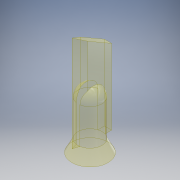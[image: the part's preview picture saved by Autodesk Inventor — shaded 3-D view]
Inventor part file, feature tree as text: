
AUTODESK INVENTOR PART (.ipt)
format: ipt  version: 2017 (Build 210142000, 142)  size: 141,824 bytes
history: native  units: mm
features: sketch x6, plane x3, extrude x3, loft x1, revolve x1
ambient origin geometry x8: Origin, YZ Plane, XZ Plane, XY Plane, X Axis, Y Axis, Z Axis, Center Point
bodies: Body1 (feature_tree)
feature tree (14):
  sketch  "Sketch1"  dims[d0=15.0mm d4=10.0mm]
  plane  "Work Plane1"
  loft  "Loft1"
  extrude  "Extrusion2"  TaperAngle=0.0deg  [1 undecoded]
  revolve  "Revolution1"  [1 undecoded]
  plane  "Work Plane2"
  extrude  "Extrusion3"  [1 undecoded]
  plane  "Work Plane3"
  extrude  "Extrusion4"  Depth=3.0mm TaperAngle=0.0deg
  sketch  "Sketch2"  dims[d5=0.0mm d6=90.0deg d7=0.0mm d8=90.0deg]
  sketch  "Sketch3"  dims[d9=10.0mm d10=15.0mm d11=0.0mm]
  sketch  "Sketch4"  dims[d12=180.0deg d13=-5.0mm]
  sketch  "Sketch6"  dims[d14=3.0mm d16=40.0mm d17=0.0mm]
  sketch  "Sketch7"  dims[d18=30.0deg d19=23.462241mm d20=7.5mm d21=0.0mm]
note: 3 required parameter values undecoded (feature->parameter linkage not recoverable at this tier; creation-order binding heuristic only, values carry confidence <= 0.55)